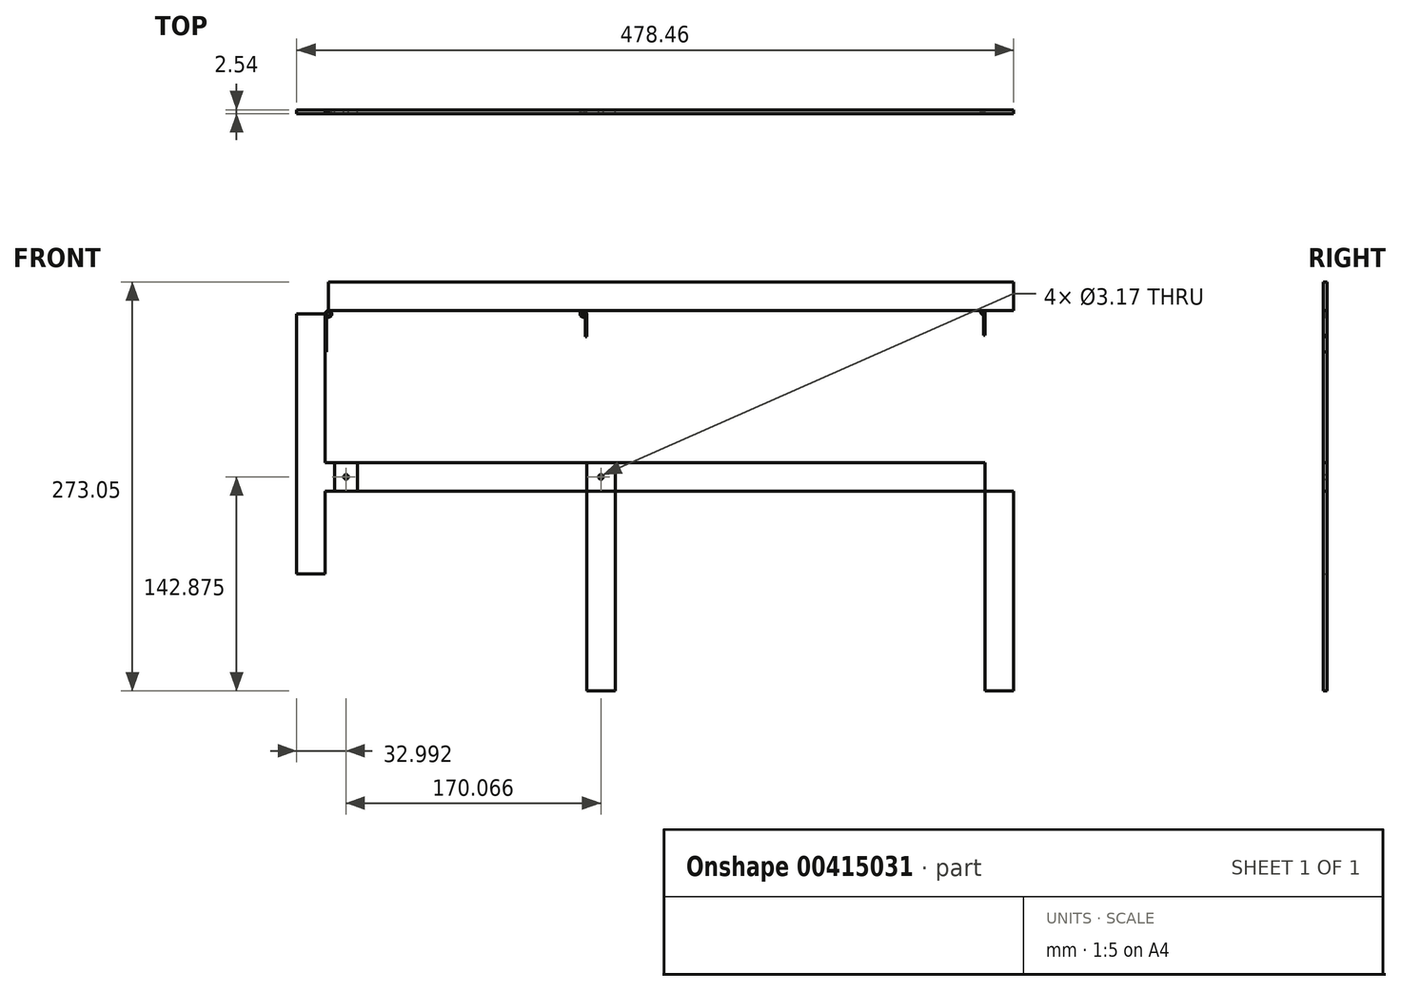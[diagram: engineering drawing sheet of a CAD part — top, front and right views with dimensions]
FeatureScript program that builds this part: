
annotation { "Feature Type Name" : "Feature", "Feature Type Description" : "" }
export const myFeature = defineFeature(function(context is Context, id is Id, definition is map)
    precondition{}
    {
        {
            var Q0;
            Q0=qCreatedBy(makeId("Front.planeOp"),FACE);
            var sketch = newSketch(context, id + "F0", { "sketchPlane" : qUnion([Q0])});
            skLineSegment(sketch, "E0.bottom", {"start": v(-228.6, 19.05) * mm, "end": v(228.6, 19.05) * mm});
            skLineSegment(sketch, "E0.top", {"start": v(-228.6, 0) * mm, "end": v(228.6, 0) * mm});
            skLineSegment(sketch, "E0.left", {"start": v(-228.6, 19.05) * mm, "end": v(-228.6, 0) * mm});
            skLineSegment(sketch, "E0.right", {"start": v(228.6, 19.05) * mm, "end": v(228.6, 0) * mm});
            skPoint(sketch, "E1", {"position": v(0, 0) * mm});
            skLineSegment(sketch, "E2.bottom", {"start": v(228.6, 0) * mm, "end": v(209.55, 0) * mm});
            skLineSegment(sketch, "E2.top", {"start": v(228.6, -254) * mm, "end": v(209.55, -254) * mm});
            skLineSegment(sketch, "E2.left", {"start": v(228.6, 0) * mm, "end": v(228.6, -254) * mm});
            skLineSegment(sketch, "E2.right", {"start": v(209.55, 0) * mm, "end": v(209.55, -254) * mm});
            skLineSegment(sketch, "E3.bottom", {"start": v(-37.28, 0) * mm, "end": v(-56.33, 0) * mm});
            skLineSegment(sketch, "E3.top", {"start": v(-37.28, -254) * mm, "end": v(-56.33, -254) * mm});
            skLineSegment(sketch, "E3.left", {"start": v(-37.28, 0) * mm, "end": v(-37.28, -254) * mm});
            skLineSegment(sketch, "E3.right", {"start": v(-56.33, 0) * mm, "end": v(-56.33, -254) * mm});
            skLineSegment(sketch, "E4.bottom", {"start": v(-249.86, -120.65) * mm, "end": v(228.6, -120.65) * mm});
            skLineSegment(sketch, "E4.top", {"start": v(-249.86, -101.6) * mm, "end": v(228.6, -101.6) * mm});
            skLineSegment(sketch, "E4.right", {"start": v(228.6, -120.65) * mm, "end": v(228.6, -101.6) * mm});
            skPoint(sketch, "E5", {"position": v(219.08, -111.12) * mm});
            skPoint(sketch, "E5.positionSnap0", {"position": v(228.6, -111.12) * mm});
            skCircle(sketch, "E6", {"center": v(219.08, -111.12) * mm, "radius": 1.59 * mm});
            skLineSegment(sketch, "E7.bottom", {"start": v(-56.33, -101.6) * mm, "end": v(-37.28, -101.6) * mm, "construction": true});
            skLineSegment(sketch, "E7.top", {"start": v(-56.33, -120.65) * mm, "end": v(-37.28, -120.65) * mm, "construction": true});
            skLineSegment(sketch, "E7.left", {"start": v(-56.33, -101.6) * mm, "end": v(-56.33, -120.65) * mm, "construction": true});
            skLineSegment(sketch, "E7.right", {"start": v(-37.28, -101.6) * mm, "end": v(-37.28, -120.65) * mm, "construction": true});
            skPoint(sketch, "E8", {"position": v(-46.8, -111.13) * mm});
            skPoint(sketch, "E8.positionSnap0", {"position": v(-56.33, -111.13) * mm});
            skPoint(sketch, "E8.positionSnap1", {"position": v(-46.8, -101.6) * mm});
            skCircle(sketch, "E9", {"center": v(-46.8, -111.13) * mm, "radius": 1.59 * mm});
            skLineSegment(sketch, "E10.bottom", {"start": v(228.6, -101.6) * mm, "end": v(209.55, -101.6) * mm, "construction": true});
            skLineSegment(sketch, "E10.top", {"start": v(228.6, -120.65) * mm, "end": v(209.55, -120.65) * mm, "construction": true});
            skLineSegment(sketch, "E10.left", {"start": v(228.6, -101.6) * mm, "end": v(228.6, -120.65) * mm, "construction": true});
            skLineSegment(sketch, "E10.right", {"start": v(209.55, -101.6) * mm, "end": v(209.55, -120.65) * mm, "construction": true});
            skPoint(sketch, "E11", {"position": v(219.08, -101.6) * mm});
            skLineSegment(sketch, "E12.bottom", {"start": v(209.55, -16.62) * mm, "end": v(208.56, -16.62) * mm});
            skLineSegment(sketch, "E12.top", {"start": v(209.55, -1.38) * mm, "end": v(208.56, -1.38) * mm});
            skLineSegment(sketch, "E12.left", {"start": v(209.55, -16.62) * mm, "end": v(209.55, -1.38) * mm});
            skLineSegment(sketch, "E12.right", {"start": v(208.56, -16.62) * mm, "end": v(208.56, -1.38) * mm});
            skLineSegment(sketch, "E13", {"start": v(208.56, -1.38) * mm, "end": v(208.17, -1.38) * mm, "construction": true});
            skArc(sketch, "E14", {"start": v(208.56, -1.38) * mm, "mid": v(208.02, -1.02) * mm, "end": v(207.87, -1.65) * mm});
            skArc(sketch, "E15", {"start": v(209.55, -1.38) * mm, "mid": v(207.11, -0.49) * mm, "end": v(208.39, -2.75) * mm});
            skLineSegment(sketch, "E16", {"start": v(207.87, -1.65) * mm, "end": v(208.39, -2.75) * mm});
            skLineSegment(sketch, "E17.bottom", {"start": v(-56.33, -17.45) * mm, "end": v(-57.34, -17.45) * mm});
            skLineSegment(sketch, "E17.top", {"start": v(-56.33, -2.2) * mm, "end": v(-57.34, -2.2) * mm});
            skLineSegment(sketch, "E17.left", {"start": v(-56.33, -17.45) * mm, "end": v(-56.33, -2.2) * mm});
            skLineSegment(sketch, "E17.right", {"start": v(-57.34, -17.45) * mm, "end": v(-57.34, -2.2) * mm});
            skLineSegment(sketch, "E18", {"start": v(-57.34, -2.2) * mm, "end": v(-58.53, -2.2) * mm, "construction": true});
            skArc(sketch, "E19", {"start": v(-57.34, -2.2) * mm, "mid": v(-59.54, -1.57) * mm, "end": v(-58.03, -3.29) * mm});
            skArc(sketch, "E20", {"start": v(-56.33, -2.2) * mm, "mid": v(-60.4, -1.02) * mm, "end": v(-57.6, -4.2) * mm});
            skLineSegment(sketch, "E21", {"start": v(-58.03, -3.29) * mm, "end": v(-57.6, -4.2) * mm});
            skLineSegment(sketch, "E22", {"start": v(208.17, -1.38) * mm, "end": v(219.08, -111.12) * mm, "construction": true});
            skLineSegment(sketch, "E23", {"start": v(-228.6, -2.2) * mm, "end": v(-216.87, -111.12) * mm, "construction": true});
            skCircle(sketch, "E24", {"center": v(-216.87, -111.12) * mm, "radius": 1.59 * mm});
            skLineSegment(sketch, "E25.bottom", {"start": v(-230.8, -2.2) * mm, "end": v(-249.86, -2.2) * mm});
            skLineSegment(sketch, "E25.top", {"start": v(-230.8, -175.86) * mm, "end": v(-249.86, -175.86) * mm});
            skLineSegment(sketch, "E25.left", {"start": v(-230.8, -2.2) * mm, "end": v(-230.8, -175.86) * mm});
            skLineSegment(sketch, "E25.right", {"start": v(-249.86, -2.2) * mm, "end": v(-249.86, -175.86) * mm});
            skLineSegment(sketch, "E26.bottom", {"start": v(-230.8, -2.2) * mm, "end": v(-229.8, -2.2) * mm});
            skLineSegment(sketch, "E26.top", {"start": v(-230.8, -27.6) * mm, "end": v(-229.8, -27.6) * mm});
            skLineSegment(sketch, "E26.left", {"start": v(-230.8, -2.2) * mm, "end": v(-230.8, -27.6) * mm});
            skLineSegment(sketch, "E26.right", {"start": v(-229.8, -2.2) * mm, "end": v(-229.8, -27.6) * mm});
            skLineSegment(sketch, "E27", {"start": v(-229.8, -2.2) * mm, "end": v(-228.6, -2.2) * mm, "construction": true});
            skArc(sketch, "E28", {"start": v(-229.8, -2.2) * mm, "mid": v(-227.6, -1.57) * mm, "end": v(-229.1, -3.29) * mm});
            skArc(sketch, "E29", {"start": v(-230.8, -2.2) * mm, "mid": v(-226.74, -1.02) * mm, "end": v(-229.53, -4.2) * mm});
            skLineSegment(sketch, "E30", {"start": v(-229.1, -3.29) * mm, "end": v(-229.53, -4.2) * mm});
            skLineSegment(sketch, "E31.bottom", {"start": v(-228.6, 0) * mm, "end": v(-203.2, 0) * mm});
            skLineSegment(sketch, "E31.top", {"start": v(-228.6, -1.02) * mm, "end": v(-203.2, -1.02) * mm});
            skLineSegment(sketch, "E31.left", {"start": v(-228.6, 0) * mm, "end": v(-228.6, -1.02) * mm});
            skLineSegment(sketch, "E31.right", {"start": v(-203.2, 0) * mm, "end": v(-203.2, -1.02) * mm});
            skLineSegment(sketch, "E32", {"start": v(-224.46, -101.6) * mm, "end": v(-224.46, -120.65) * mm});
            skLineSegment(sketch, "E33", {"start": v(-209.22, -101.6) * mm, "end": v(-209.22, -120.65) * mm});
            skSolve(sketch);
        }
        {
            var Q0;
            {var subQ0=sQuery(id+"F0.wireOp",EDGE,"E4.right");Q0=makeQuery(id+"F0.imprint","IMPRINT",FACE,{"disambiguationData":[TD([[makeQuery(id+"F0.imprint","IMPRINT",EDGE,{"derivedFrom":subQ0}),1.0]])]});}
            var Q1;
            {var subQ0=sQuery(id+"F0.wireOp",EDGE,"E4.bottom");var subQ1=sQuery(id+"F0.wireOp",EDGE,"E2.right");var subQ2=makeQuery(id+"F0.imprint","INTERSECT",VERTEX,{"derivedFrom":[subQ1,subQ0]});Q1=makeQuery(id+"F0.imprint","IMPRINT",FACE,{"disambiguationData":[TD([[makeQuery(id+"F0.imprint","IMPRINT",EDGE,{"disambiguationData":[TD([[subQ2,1.0]])],"derivedFrom":subQ1}),-1.0]])]});}
            var Q2;
            Q2=makeQuery(id+"F0.imprint","IMPRINT",FACE,{"disambiguationData":[TD([[makeQuery(id+"F0.imprint","IMPRINT",EDGE,{"derivedFrom":sQuery(id+"F0.wireOp",EDGE,"E9")}),-1.0]])]});
            var Q3;
            {var subQ5=sQuery(id+"F0.wireOp",EDGE,"E33");Q3=makeQuery(id+"F0.imprint","IMPRINT",FACE,{"disambiguationData":[TD([[makeQuery(id+"F0.imprint","IMPRINT",EDGE,{"derivedFrom":subQ5}),1.0]])]});}
            var Q4;
            Q4=makeQuery(id+"F0.imprint","IMPRINT",FACE,{"disambiguationData":[TD([[makeQuery(id+"F0.imprint","IMPRINT",EDGE,{"derivedFrom":sQuery(id+"F0.wireOp",EDGE,"E24")}),-1.0]])]});
            extrude(context, id + "F1", {"entities" : qUnion([Q0, Q1, Q2, Q3, Q4]), "depth" : 2.54 * mm});
        }
        {
            var Q0;
            Q0=makeQuery(id+"F0.imprint","IMPRINT",FACE,{"disambiguationData":[TD([[makeQuery(id+"F0.imprint","IMPRINT",EDGE,{"derivedFrom":sQuery(id+"F0.wireOp",EDGE,"E0.bottom")}),-1.0]])]});
            extrude(context, id + "F2", {"entities" : qUnion([Q0]), "depth" : 2.54 * mm});
        }
        {
            var Q0;
            {var subQ1=sQuery(id+"F0.wireOp",EDGE,"E2.bottom");Q0=makeQuery(id+"F0.imprint","IMPRINT",FACE,{"disambiguationData":[TD([[makeQuery(id+"F0.imprint","IMPRINT",EDGE,{"derivedFrom":subQ1}),1.0]])]});}
            var Q1;
            {var subQ0=sQuery(id+"F0.wireOp",EDGE,"E4.right");Q1=makeQuery(id+"F0.imprint","IMPRINT",FACE,{"disambiguationData":[TD([[makeQuery(id+"F0.imprint","IMPRINT",EDGE,{"derivedFrom":subQ0}),1.0]])]});}
            var Q2;
            {var subQ0=sQuery(id+"F0.wireOp",EDGE,"E2.top");Q2=makeQuery(id+"F0.imprint","IMPRINT",FACE,{"disambiguationData":[TD([[makeQuery(id+"F0.imprint","IMPRINT",EDGE,{"derivedFrom":subQ0}),-1.0]])]});}
            extrude(context, id + "F3", {"entities" : qUnion([Q0, Q1, Q2]), "depth" : 2.54 * mm});
        }
        {
            var Q0;
            {var subQ5=sQuery(id+"F0.wireOp",EDGE,"E3.bottom");Q0=makeQuery(id+"F0.imprint","IMPRINT",FACE,{"disambiguationData":[TD([[makeQuery(id+"F0.imprint","IMPRINT",EDGE,{"derivedFrom":subQ5}),1.0]])]});}
            var Q1;
            Q1=makeQuery(id+"F0.imprint","IMPRINT",FACE,{"disambiguationData":[TD([[makeQuery(id+"F0.imprint","IMPRINT",EDGE,{"derivedFrom":sQuery(id+"F0.wireOp",EDGE,"E9")}),-1.0]])]});
            var Q2;
            {var subQ0=sQuery(id+"F0.wireOp",EDGE,"E3.top");Q2=makeQuery(id+"F0.imprint","IMPRINT",FACE,{"disambiguationData":[TD([[makeQuery(id+"F0.imprint","IMPRINT",EDGE,{"derivedFrom":subQ0}),-1.0]])]});}
            extrude(context, id + "F4", {"entities" : qUnion([Q0, Q1, Q2]), "depth" : 2.54 * mm});
        }
        {
            var Q0;
            {var subQ6=sQuery(id+"F0.wireOp",EDGE,"E25.bottom");Q0=makeQuery(id+"F0.imprint","IMPRINT",FACE,{"disambiguationData":[TD([[makeQuery(id+"F0.imprint","IMPRINT",EDGE,{"derivedFrom":subQ6}),1.0]])]});}
            var Q1;
            {var subQ0=sQuery(id+"F0.wireOp",EDGE,"E25.right");var subQ1=sQuery(id+"F0.wireOp",EDGE,"E4.bottom");var subQ2=makeQuery(id+"F0.imprint","INTERSECT",VERTEX,{"derivedFrom":[subQ1,subQ0]});Q1=makeQuery(id+"F0.imprint","IMPRINT",FACE,{"disambiguationData":[TD([[makeQuery(id+"F0.imprint","IMPRINT",EDGE,{"disambiguationData":[TD([[subQ2,-1.0]])],"derivedFrom":subQ1}),1.0]])]});}
            var Q2;
            {var subQ5=sQuery(id+"F0.wireOp",EDGE,"E25.top");Q2=makeQuery(id+"F0.imprint","IMPRINT",FACE,{"disambiguationData":[TD([[makeQuery(id+"F0.imprint","IMPRINT",EDGE,{"derivedFrom":subQ5}),-1.0]])]});}
            var Q3;
            {var subQ0=sQuery(id+"F0.wireOp",EDGE,"E32");Q3=makeQuery(id+"F0.imprint","IMPRINT",FACE,{"disambiguationData":[TD([[makeQuery(id+"F0.imprint","IMPRINT",EDGE,{"derivedFrom":subQ0}),-1.0]])]});}
            var Q4;
            Q4=makeQuery(id+"F0.imprint","IMPRINT",FACE,{"disambiguationData":[TD([[makeQuery(id+"F0.imprint","IMPRINT",EDGE,{"derivedFrom":sQuery(id+"F0.wireOp",EDGE,"E24")}),-1.0]])]});
            extrude(context, id + "F5", {"entities" : qUnion([Q0, Q1, Q2, Q3, Q4]), "depth" : 2.54 * mm});
        }
        {
            var Q0;
            Q0=makeQuery(id+"F0.imprint","IMPRINT",FACE,{"disambiguationData":[TD([[makeQuery(id+"F0.imprint","IMPRINT",EDGE,{"derivedFrom":sQuery(id+"F0.wireOp",EDGE,"E12.bottom")}),-1.0]])]});
            var Q1;
            {var subQ1=sQuery(id+"F0.wireOp",EDGE,"E12.top");Q1=makeQuery(id+"F0.imprint","IMPRINT",FACE,{"disambiguationData":[TD([[makeQuery(id+"F0.imprint","IMPRINT",EDGE,{"derivedFrom":subQ1}),-1.0]])]});}
            extrude(context, id + "F6", {"entities" : qUnion([Q0, Q1]), "depth" : 2.54 * mm});
        }
        {
            var Q0;
            Q0=makeQuery(id+"F0.imprint","IMPRINT",FACE,{"disambiguationData":[TD([[makeQuery(id+"F0.imprint","IMPRINT",EDGE,{"derivedFrom":sQuery(id+"F0.wireOp",EDGE,"E17.bottom")}),-1.0]])]});
            var Q1;
            {var subQ1=sQuery(id+"F0.wireOp",EDGE,"E17.top");Q1=makeQuery(id+"F0.imprint","IMPRINT",FACE,{"disambiguationData":[TD([[makeQuery(id+"F0.imprint","IMPRINT",EDGE,{"derivedFrom":subQ1}),-1.0]])]});}
            extrude(context, id + "F7", {"entities" : qUnion([Q0, Q1]), "depth" : 2.54 * mm});
        }
        {
            var Q0;
            {var subQ0=sQuery(id+"F0.wireOp",EDGE,"E31.bottom");Q0=makeQuery(id+"F0.imprint","IMPRINT",FACE,{"disambiguationData":[TD([[makeQuery(id+"F0.imprint","IMPRINT",EDGE,{"derivedFrom":subQ0}),-1.0]])]});}
            var Q1;
            {var subQ0=sQuery(id+"F0.wireOp",EDGE,"E30");Q1=makeQuery(id+"F0.imprint","IMPRINT",FACE,{"disambiguationData":[TD([[makeQuery(id+"F0.imprint","IMPRINT",EDGE,{"derivedFrom":subQ0}),1.0]])]});}
            var Q2;
            {var subQ0=sQuery(id+"F0.wireOp",EDGE,"E31.left");Q2=makeQuery(id+"F0.imprint","IMPRINT",FACE,{"disambiguationData":[TD([[makeQuery(id+"F0.imprint","IMPRINT",EDGE,{"derivedFrom":subQ0}),1.0]])]});}
            var Q3;
            {var subQ0=sQuery(id+"F0.wireOp",EDGE,"E26.bottom");Q3=makeQuery(id+"F0.imprint","IMPRINT",FACE,{"disambiguationData":[TD([[makeQuery(id+"F0.imprint","IMPRINT",EDGE,{"derivedFrom":subQ0}),1.0]])]});}
            var Q4;
            Q4=makeQuery(id+"F0.imprint","IMPRINT",FACE,{"disambiguationData":[TD([[makeQuery(id+"F0.imprint","IMPRINT",EDGE,{"derivedFrom":sQuery(id+"F0.wireOp",EDGE,"E26.bottom")}),-1.0]])]});
            extrude(context, id + "F8", {"entities" : qUnion([Q0, Q1, Q2, Q3, Q4]), "depth" : 2.54 * mm});
        }
    });
